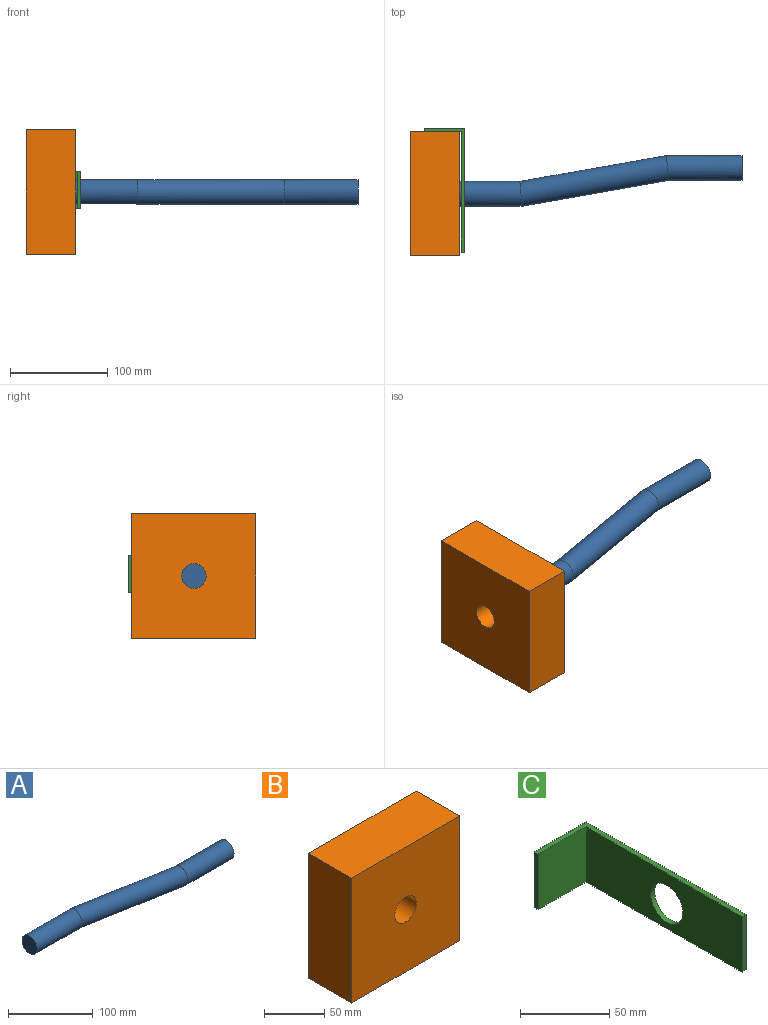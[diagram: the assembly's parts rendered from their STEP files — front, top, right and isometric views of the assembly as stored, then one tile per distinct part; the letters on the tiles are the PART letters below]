
ASSEMBLY  parts=3 mates=2
PART A: 5 faces, bbox 302.5x51.9x25.4 mm
  f0: plane 25.4x25.4mm, normal (1,0,0), area 506.7mm2, adj f2
  f1: plane 25.4x25.4mm, normal (-1,0,0), area 506.7mm2, adj f4
  f2: cylinder r=12.7mm len=77.31mm, axis (1,0,0), area 6080.5mm2, adj f0,f3
  f3: cylinder r=12.7mm len=156.68mm, axis (0.98,-0.17,0), area 12161mm2, adj f2,f4
  f4: cylinder r=12.7mm len=77.31mm, axis (1,0,0), area 6080.5mm2, adj f1,f3
PART B: 7 faces, bbox 127x50.8x127 mm
  f0: plane 127x50.8mm, normal (1,0,0), area 6451.6mm2, adj f1,f3,f5,f6
  f1: plane 127x50.8mm, normal (0,0,1), area 6451.6mm2, adj f0,f2,f5,f6
  f2: plane 127x50.8mm, normal (-1,0,0), area 6451.6mm2, adj f1,f3,f5,f6
  f3: plane 127x50.8mm, normal (0,0,-1), area 6451.6mm2, adj f0,f2,f5,f6
  f4: cylinder r=12.7mm len=50.8mm, axis (0,1,0), area 4053.7mm2, adj f5,f6
  f5: plane 127x127mm, normal (0,-1,0), area 15622.3mm2, adj f0,f1,f2,f3,f4
  f6: plane 127x127mm, normal (0,1,0), area 15622.3mm2, adj f0,f1,f2,f3,f4
PART C: 9 faces, bbox 41.3x127x38.1 mm
  f0: plane 123.83x38.1mm, normal (-1,0,0), area 4211mm2, adj f2,f3,f4,f7,f8
  f1: plane 41.28x38.1mm, normal (0,1,0), area 1572.6mm2, adj f2,f4,f5,f6
  f2: plane 127x41.28mm, normal (0,0,1), area 524.2mm2, adj f0,f1,f3,f5,f6,f7
  f3: plane 38.1x3.18mm, normal (0,-1,0), area 121mm2, adj f0,f2,f4,f5
  f4: plane 127x41.28mm, normal (0,0,-1), area 524.2mm2, adj f0,f1,f3,f5,f6,f7
  f5: plane 127x38.1mm, normal (1,0,0), area 4332mm2, adj f1,f2,f3,f4,f8
  f6: plane 38.1x3.18mm, normal (-1,0,0), area 121mm2, adj f1,f2,f4,f7
  f7: plane 38.1x38.1mm, normal (0,-1,0), area 1451.6mm2, adj f0,f2,f4,f6
  f8: cylinder r=12.7mm len=25.4mm, axis (-1,0,0), area 253.4mm2, adj f0,f5
PLACE A rot(axis=(0,1,0),180deg) t=(330.75,76.48,59.36)mm
PLACE B rot(axis=(-0.58,0.58,0.58),120deg) t=(293.42,76.48,59.36)mm
PLACE C rot(axis=(0.01,-1,-0.01),0deg) t=(345.87,143.79,80.3)mm
MATE slider C.f8 <-> A.f2  axis (1,0,0) through (349.04,76.48,59.36)mm
MATE slider B.f4 <-> A.f2  axis (1,0,0) through (344.22,76.48,59.36)mm
